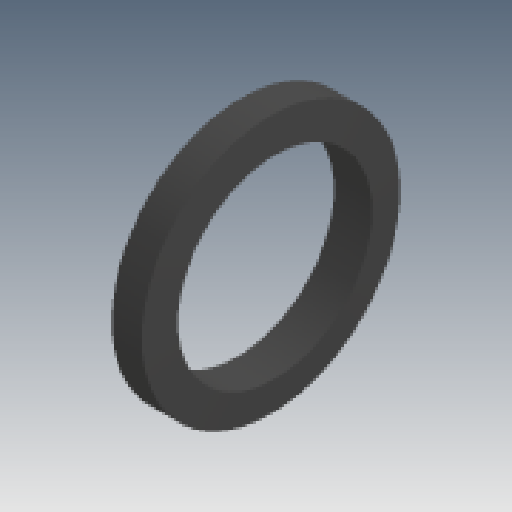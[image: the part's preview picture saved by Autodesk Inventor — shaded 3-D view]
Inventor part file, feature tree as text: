
AUTODESK INVENTOR PART (.ipt)
format: ipt  version: 2025 (Build 290162000, 162)  size: 100,864 bytes
history: native  units: mm
features: reference x10, other x2, revolve x1, sketch x1
ambient origin geometry x8: Origin, YZ Plane, XZ Plane, XY Plane, X Axis, Y Axis, Z Axis, Center Point
bodies: 实体1 (feature_tree)
feature tree (14):
  revolve  "旋转1"  Angle=90.0deg
  sketch  "草图1"  dims[d0=22.5mm d1=90.0deg]
  reference  "参考1"
  reference  "参考2"
  reference  "参考3"
  reference  "参考4"
  reference  "参考5"
  reference  "参考6"
  reference  "参考7"
  reference  "参考8"
  reference  "参考9"
  reference  "参考10"
  other  "齿轮箱.iam"
  other  "低速轴承透盖"
